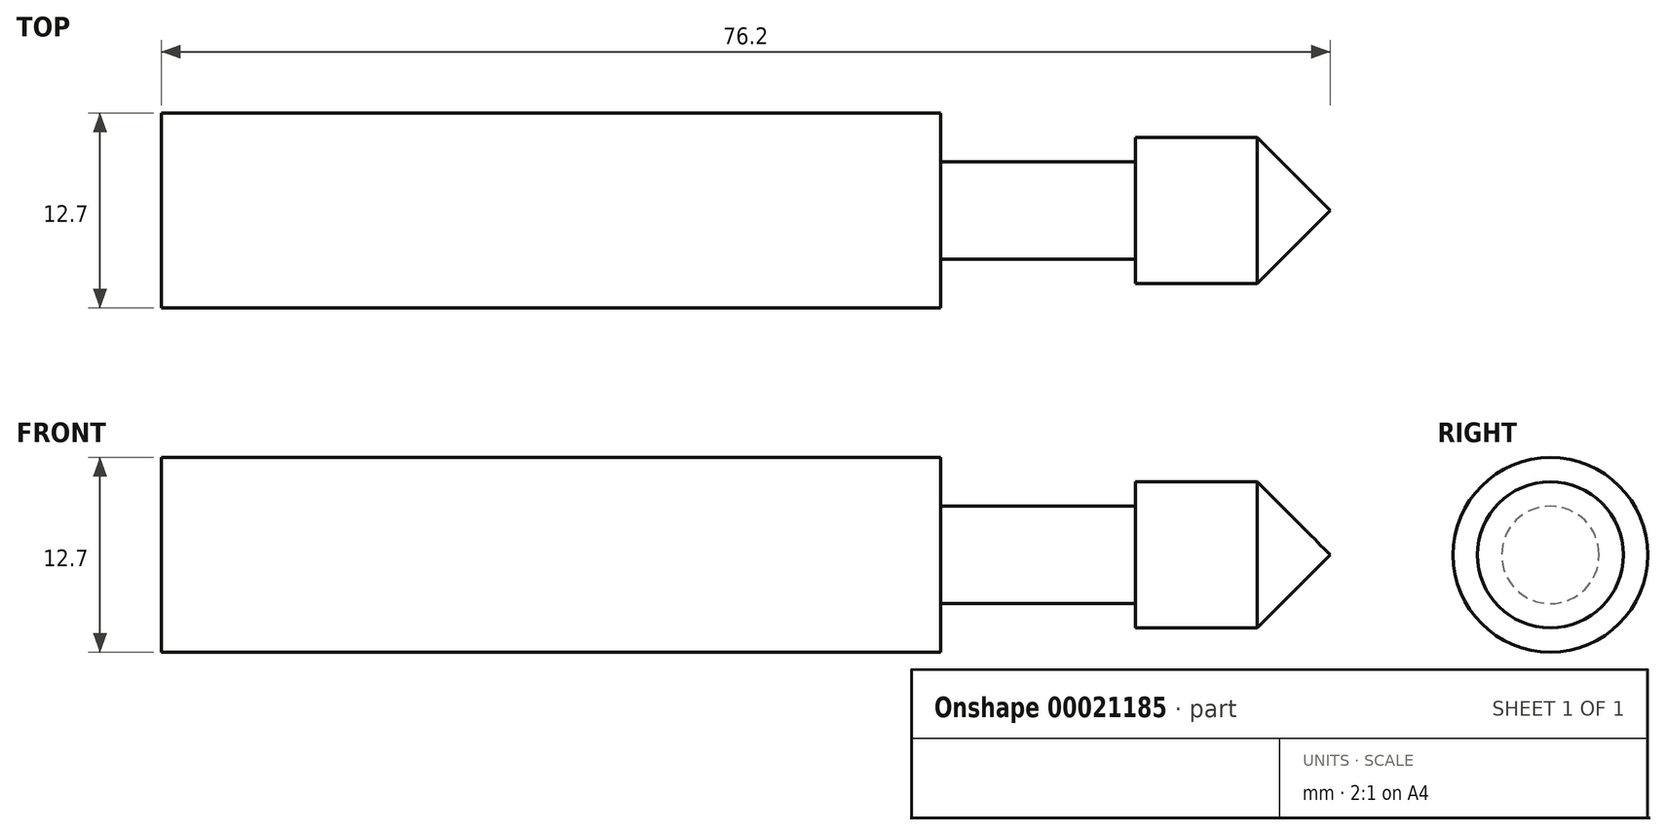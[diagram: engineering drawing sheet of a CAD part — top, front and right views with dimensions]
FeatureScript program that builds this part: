
annotation { "Feature Type Name" : "Feature", "Feature Type Description" : "" }
export const myFeature = defineFeature(function(context is Context, id is Id, definition is map)
    precondition{}
    {
        {
            var Q0;
            Q0=qCreatedBy(makeId("Top.planeOp"),FACE);
            var sketch = newSketch(context, id + "F0", { "sketchPlane" : qUnion([Q0])});
            skLineSegment(sketch, "E0", {"start": v(4.76, 0) * mm, "end": v(-71.44, 0) * mm});
            skLineSegment(sketch, "E1", {"start": v(0, 0) * mm, "end": v(0, 4.76) * mm});
            skLineSegment(sketch, "E2", {"start": v(0, 4.76) * mm, "end": v(-7.94, 4.76) * mm});
            skLineSegment(sketch, "E3", {"start": v(-7.94, 4.76) * mm, "end": v(-7.94, 3.17) * mm});
            skLineSegment(sketch, "E4", {"start": v(-7.94, 3.17) * mm, "end": v(-20.64, 3.17) * mm});
            skLineSegment(sketch, "E5", {"start": v(-20.64, 3.17) * mm, "end": v(-20.64, 6.35) * mm});
            skLineSegment(sketch, "E6", {"start": v(-20.64, 6.35) * mm, "end": v(-71.44, 6.35) * mm});
            skLineSegment(sketch, "E7", {"start": v(-71.44, 6.35) * mm, "end": v(-71.44, 0) * mm});
            skLineSegment(sketch, "E8", {"start": v(9.85, 0) * mm, "end": v(-41.71, 0) * mm, "construction": true});
            skLineSegment(sketch, "E9", {"start": v(0, 4.76) * mm, "end": v(4.76, 0) * mm});
            skSolve(sketch);
        }
        {
            var Q0;
            Q0 = qSketchRegion(id + "F0", true);
            var Q1;
            Q1=sQuery(id+"F0.wireOp",EDGE,"E0");
            revolve(context, id + "F1", {"entities" : qUnion([Q0]), "axis" : qUnion([Q1]), "revolveType" : RevolveType.FULL});
        }
    });
